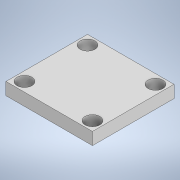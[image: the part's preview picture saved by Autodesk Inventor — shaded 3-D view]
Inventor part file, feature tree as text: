
AUTODESK INVENTOR PART (.ipt)
format: ipt  version: 2020.2 (Build 242310000, 310)  size: 117,248 bytes
history: native  units: in
note: dims shown in document units (in); Inventor stores cm internally (conversion verified against a paired STEP export)
features: sketch x2, extrude x1, hole x1
ambient origin geometry x8: Origin, YZ Plane, XZ Plane, XY Plane, X Axis, Y Axis, Z Axis, Center Point
bodies: Solid1 (feature_tree)
feature tree (4):
  extrude  "Extrusion1"  Depth=0.66in
  hole  "Hole1"  [1 undecoded]
  sketch  "Sketch1"  dims[d0=0.7in d1=0.66in]
  sketch  "Sketch2"  dims[d2=0.1in d3=0.0in d4=0.15in d5=0.15in d6=0.15in d7=0.15in d8=0.15in d9=0.15in d10=0.15in d11=0.15in d12=0.12in d13=0.75in d14=0.375in d15=0.25in d16=0.5635in d17=0.4in d18=0.8108in]
note: 1 required parameter value undecoded (feature->parameter linkage not recoverable at this tier; creation-order binding heuristic only, values carry confidence <= 0.55)
